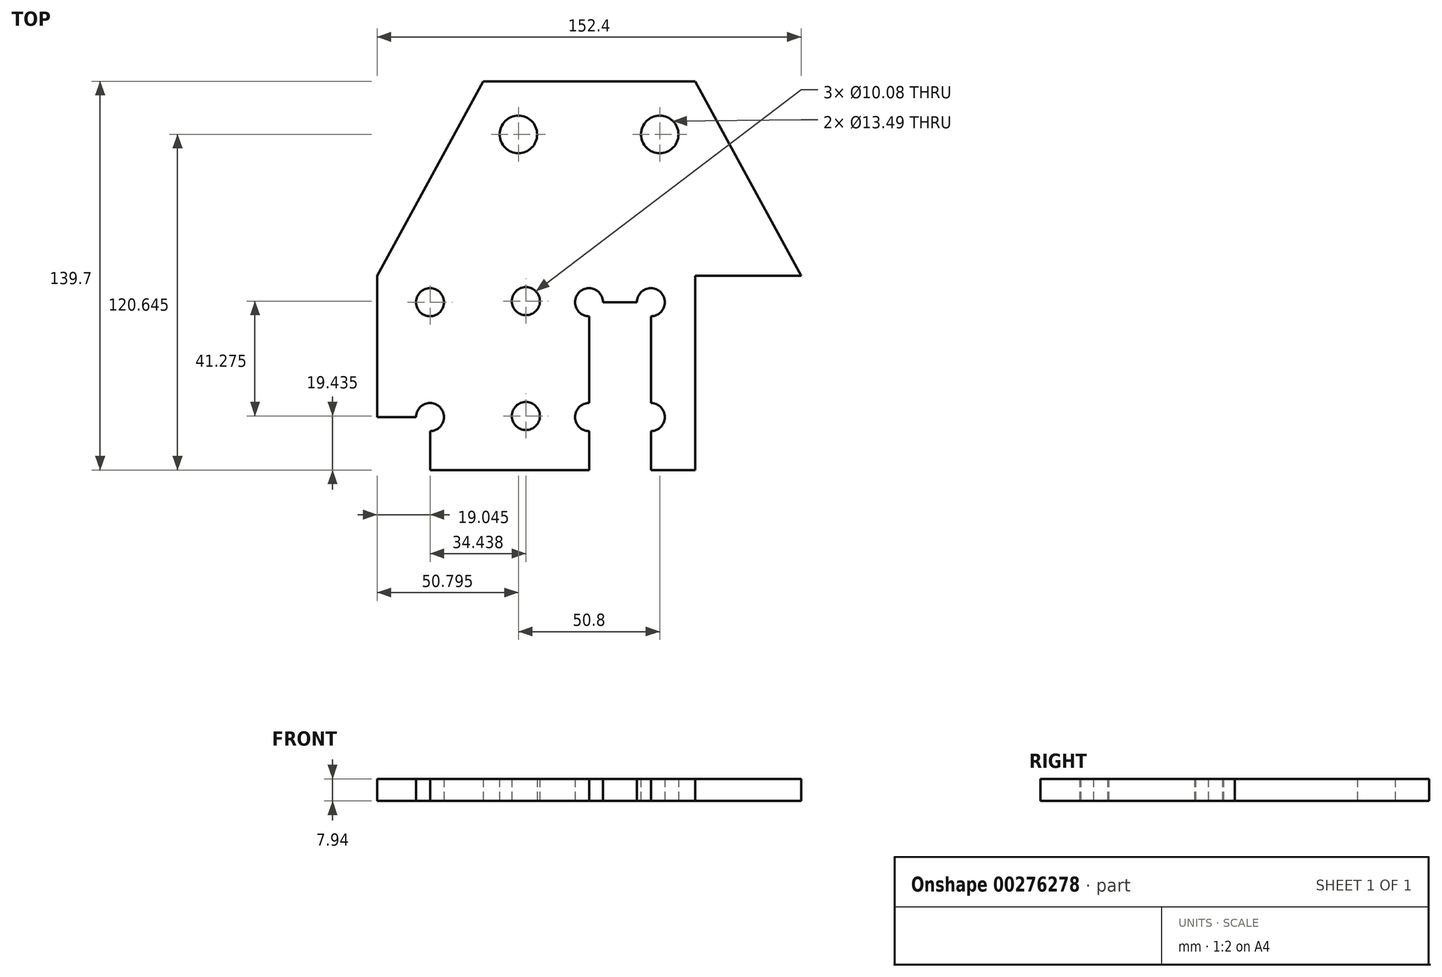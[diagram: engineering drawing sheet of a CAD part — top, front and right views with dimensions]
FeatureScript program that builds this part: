
annotation { "Feature Type Name" : "Feature", "Feature Type Description" : "" }
export const myFeature = defineFeature(function(context is Context, id is Id, definition is map)
    precondition{}
    {
        {
            var Q0;
            Q0=qCreatedBy(makeId("Top.planeOp"),FACE);
            var sketch = newSketch(context, id + "F0", { "sketchPlane" : qUnion([Q0])});
            skLineSegment(sketch, "E0.bottom", {"start": v(-76.05, -60.71) * mm, "end": v(76.35, -60.71) * mm});
            skLineSegment(sketch, "E0.top", {"start": v(-76.05, 78.99) * mm, "end": v(76.35, 78.99) * mm});
            skLineSegment(sketch, "E0.left", {"start": v(-76.05, -60.71) * mm, "end": v(-76.05, 78.99) * mm});
            skLineSegment(sketch, "E0.right", {"start": v(76.35, -60.71) * mm, "end": v(76.35, 78.99) * mm});
            skLineSegment(sketch, "E1", {"start": v(-76.05, -60.71) * mm, "end": v(-76.05, 9.14) * mm});
            skLineSegment(sketch, "E2", {"start": v(-76.05, 9.14) * mm, "end": v(76.35, 9.14) * mm});
            skLineSegment(sketch, "E3", {"start": v(76.35, 9.14) * mm, "end": v(76.35, -60.71) * mm});
            skLineSegment(sketch, "E4.bottom", {"start": v(-37.95, 78.99) * mm, "end": v(38.25, 78.99) * mm});
            skLineSegment(sketch, "E4.top", {"start": v(-37.95, -60.71) * mm, "end": v(38.25, -60.71) * mm});
            skLineSegment(sketch, "E4.left", {"start": v(-37.95, 78.99) * mm, "end": v(-37.95, -60.71) * mm});
            skLineSegment(sketch, "E4.right", {"start": v(38.25, 78.99) * mm, "end": v(38.25, -60.71) * mm});
            skLineSegment(sketch, "E5", {"start": v(-76.05, 78.99) * mm, "end": v(-37.95, 78.99) * mm});
            skLineSegment(sketch, "E6", {"start": v(-76.05, 9.14) * mm, "end": v(-37.95, 78.99) * mm});
            skLineSegment(sketch, "E7", {"start": v(38.25, 78.99) * mm, "end": v(76.35, 9.14) * mm});
            skPoint(sketch, "E8", {"position": v(38.25, 78.99) * mm});
            skLineSegment(sketch, "E9", {"start": v(-25.25, 59.94) * mm, "end": v(-25.25, 78.99) * mm});
            skLineSegment(sketch, "E10", {"start": v(25.55, 59.94) * mm, "end": v(25.55, 78.99) * mm});
            skLineSegment(sketch, "E11", {"start": v(-25.25, 59.94) * mm, "end": v(-37.95, 59.94) * mm});
            skLineSegment(sketch, "E12", {"start": v(25.55, 59.94) * mm, "end": v(38.25, 59.94) * mm});
            skLineSegment(sketch, "E13", {"start": v(-57, -0.39) * mm, "end": v(-57, -41.66) * mm});
            skLineSegment(sketch, "E14", {"start": v(-57, -41.66) * mm, "end": v(-76.05, -41.66) * mm});
            skLineSegment(sketch, "E15", {"start": v(-57, -41.66) * mm, "end": v(-57, -60.71) * mm});
            skLineSegment(sketch, "E16", {"start": v(57.3, -0.39) * mm, "end": v(57.3, -41.66) * mm});
            skLineSegment(sketch, "E17", {"start": v(57.3, -41.66) * mm, "end": v(57.3, -60.71) * mm});
            skLineSegment(sketch, "E18", {"start": v(57.3, -60.71) * mm, "end": v(76.35, -60.71) * mm});
            skLineSegment(sketch, "E19", {"start": v(-76.05, -60.71) * mm, "end": v(0.15, -60.71) * mm});
            skLineSegment(sketch, "E20", {"start": v(0.15, -0.39) * mm, "end": v(0.15, -41.66) * mm});
            skLineSegment(sketch, "E21", {"start": v(0.15, -41.66) * mm, "end": v(0.15, -60.71) * mm});
            skLineSegment(sketch, "E22", {"start": v(22.37, -0.39) * mm, "end": v(22.37, -41.66) * mm});
            skLineSegment(sketch, "E23", {"start": v(22.37, -41.66) * mm, "end": v(22.37, -60.71) * mm});
            skLineSegment(sketch, "E24", {"start": v(0.15, -0.39) * mm, "end": v(22.37, -0.39) * mm});
            skLineSegment(sketch, "E25", {"start": v(-22.57, 0) * mm, "end": v(-22.57, -41.28) * mm});
            skLineSegment(sketch, "E26", {"start": v(-22.57, -41.28) * mm, "end": v(-22.57, -60.33) * mm});
            skLineSegment(sketch, "E27", {"start": v(-22.57, 0) * mm, "end": v(-0.34, 0) * mm});
            skSolve(sketch);
        }
        {
            var Q0;
            {var subQ0=sQuery(id+"F0.wireOp",EDGE,"E6");Q0=makeQuery(id+"F0.imprint","IMPRINT",FACE,{"disambiguationData":[TD([[makeQuery(id+"F0.imprint","IMPRINT",EDGE,{"derivedFrom":subQ0}),-1.0]])]});}
            var Q1;
            {var subQ0=sQuery(id+"F0.wireOp",EDGE,"E1");Q1=makeQuery(id+"F0.imprint","IMPRINT",FACE,{"disambiguationData":[TD([[makeQuery(id+"F0.imprint","IMPRINT",EDGE,{"derivedFrom":subQ0}),-1.0]])]});}
            var Q2;
            {var subQ5=sQuery(id+"F0.wireOp",EDGE,"E4.top");Q2=makeQuery(id+"F0.imprint","IMPRINT",FACE,{"disambiguationData":[TD([[makeQuery(id+"F0.imprint","IMPRINT",EDGE,{"derivedFrom":subQ5}),1.0]])]});}
            var Q3;
            {var subQ3=sQuery(id+"F0.wireOp",EDGE,"E2");var subQ5=sQuery(id+"F0.wireOp",EDGE,"E4.left");var subQ6=makeQuery(id+"F0.imprint","INTERSECT",VERTEX,{"derivedFrom":[subQ3,subQ5]});Q3=makeQuery(id+"F0.imprint","IMPRINT",FACE,{"disambiguationData":[TD([[makeQuery(id+"F0.imprint","IMPRINT",EDGE,{"disambiguationData":[TD([[subQ6,-1.0]])],"derivedFrom":subQ3}),1.0]])]});}
            var Q4;
            {var subQ0=sQuery(id+"F0.wireOp",EDGE,"E9");var subQ1=sQuery(id+"F0.wireOp",EDGE,"LTa7V2wM-ZibM-cuZf-cZ65-yHtlyJLLMwwq");var subQ2=makeQuery(id+"F0.imprint","INTERSECT",VERTEX,{"derivedFrom":[subQ1,subQ0]});Q4=makeQuery(id+"F0.imprint","IMPRINT",FACE,{"disambiguationData":[TD([[makeQuery(id+"F0.imprint","IMPRINT",EDGE,{"disambiguationData":[TD([[subQ2,-1.0]])],"derivedFrom":subQ1}),-1.0]])]});}
            var Q5;
            {var subQ0=sQuery(id+"F0.wireOp",EDGE,"E10");var subQ1=sQuery(id+"F0.wireOp",EDGE,"ef0b0393-9919-4fb4-960b-99aeebce1d35");var subQ2=makeQuery(id+"F0.imprint","INTERSECT",VERTEX,{"derivedFrom":[subQ1,subQ0]});Q5=makeQuery(id+"F0.imprint","IMPRINT",FACE,{"disambiguationData":[TD([[makeQuery(id+"F0.imprint","IMPRINT",EDGE,{"disambiguationData":[TD([[subQ2,1.0]])],"derivedFrom":subQ1}),-1.0]])]});}
            var Q6;
            {var subQ0=sQuery(id+"F0.wireOp",EDGE,"E7");Q6=makeQuery(id+"F0.imprint","IMPRINT",FACE,{"disambiguationData":[TD([[makeQuery(id+"F0.imprint","IMPRINT",EDGE,{"derivedFrom":subQ0}),-1.0]])]});}
            var Q7;
            {var subQ0=sQuery(id+"F0.wireOp",EDGE,"E3");Q7=makeQuery(id+"F0.imprint","IMPRINT",FACE,{"disambiguationData":[TD([[makeQuery(id+"F0.imprint","IMPRINT",EDGE,{"derivedFrom":subQ0}),-1.0]])]});}
            var Q8;
            {var subQ7=sQuery(id+"F0.wireOp",EDGE,"E14");Q8=makeQuery(id+"F0.imprint","IMPRINT",FACE,{"disambiguationData":[TD([[makeQuery(id+"F0.imprint","IMPRINT",EDGE,{"derivedFrom":subQ7}),-1.0]])]});}
            var Q9;
            {var subQ3=sQuery(id+"F0.wireOp",EDGE,"E9");Q9=makeQuery(id+"F0.imprint","IMPRINT",FACE,{"disambiguationData":[TD([[makeQuery(id+"F0.imprint","IMPRINT",EDGE,{"derivedFrom":subQ3}),1.0]])]});}
            var Q10;
            {var subQ3=sQuery(id+"F0.wireOp",EDGE,"E10");Q10=makeQuery(id+"F0.imprint","IMPRINT",FACE,{"disambiguationData":[TD([[makeQuery(id+"F0.imprint","IMPRINT",EDGE,{"derivedFrom":subQ3}),-1.0]])]});}
            var Q11;
            Q11=makeQuery(id+"F0.imprint","IMPRINT",FACE,{"disambiguationData":[TD([[makeQuery(id+"F0.imprint","IMPRINT",EDGE,{"derivedFrom":sQuery(id+"F0.wireOp",EDGE,"E20")}),-1.0]])]});
            extrude(context, id + "F1", {"entities" : qUnion([Q0, Q1, Q2, Q3, Q4, Q5, Q6, Q7, Q8, Q9, Q10, Q11]), "depth" : 7.94 * mm});
        }
        {
            var Q0;
            Q0=sQuery(id+"F0.wireOp",VERTEX,"E13.start");
            var Q1;
            Q1=sQuery(id+"F0.wireOp",VERTEX,"E14.start");
            var Q2;
            Q2=sQuery(id+"F0.wireOp",VERTEX,"E20.start");
            var Q3;
            Q3=sQuery(id+"F0.wireOp",VERTEX,"E21.start");
            var Q4;
            Q4=sQuery(id+"F0.wireOp",VERTEX,"E16.start");
            var Q5;
            Q5=sQuery(id+"F0.wireOp",VERTEX,"E17.start");
            var Q6;
            Q6=sQuery(id+"F0.wireOp",VERTEX,"E25.start");
            var Q7;
            Q7=sQuery(id+"F0.wireOp",VERTEX,"E26.start");
            var Q8;
            Q8=sQuery(id+"F0.wireOp",VERTEX,"E23.start");
            var Q9;
            Q9=sQuery(id+"F0.wireOp",VERTEX,"E22.start");
            var Q10;
            Q10=makeQuery(id+"F1.opExtrude","SWEPT_BODY",BODY,{"disambiguationData":[OSD([sQuery(id+"F0.wireOp",EDGE,"E0.bottom"),sQuery(id+"F0.wireOp",EDGE,"E1"),sQuery(id+"F0.wireOp",EDGE,"E3"),sQuery(id+"F0.wireOp",EDGE,"E4.bottom"),sQuery(id+"F0.wireOp",EDGE,"E4.top"),sQuery(id+"F0.wireOp",EDGE,"E6"),sQuery(id+"F0.wireOp",EDGE,"E7"),sQuery(id+"F0.wireOp",EDGE,"LTa7V2wM-ZibM-cuZf-cZ65-yHtlyJLLMwwq"),sQuery(id+"F0.wireOp",EDGE,"ef0b0393-9919-4fb4-960b-99aeebce1d35"),sQuery(id+"F0.wireOp",EDGE,"E18"),sQuery(id+"F0.wireOp",EDGE,"E19")])]});
            hole(context, id + "F2", {"style" : HoleStyle.SIMPLE, "endStyle" : HoleEndStyle.THROUGH, "oppositeDirection" : true, "standardTappedOrClearance" : lookupTablePath({ "standard" : "ANSI", "fit" : "Normal (ASME)", "size" : "3/8", "type" : "Clearance" }), "standardBlindInLast" : lookupTablePath({ "fit" : "Free", "standard" : "ANSI", "size" : "3/8", "type" : "Clearance" }), "holeDiameter" : 10.08 * mm, "tappedDepth" : 12.7 * mm, "tapClearance" : 3, "locations" : qUnion([Q0, Q1, Q2, Q3, Q4, Q5, Q6, Q7, Q8, Q9]), "scope" : qUnion([Q10])});
        }
        {
            var Q0;
            Q0=sQuery(id+"F0.wireOp",VERTEX,"E9.start");
            var Q1;
            Q1=sQuery(id+"F0.wireOp",VERTEX,"E12.start");
            var Q2;
            Q2=makeQuery(id+"F1.opExtrude","SWEPT_BODY",BODY,{"disambiguationData":[OSD([sQuery(id+"F0.wireOp",EDGE,"E0.bottom"),sQuery(id+"F0.wireOp",EDGE,"E1"),sQuery(id+"F0.wireOp",EDGE,"E3"),sQuery(id+"F0.wireOp",EDGE,"E4.bottom"),sQuery(id+"F0.wireOp",EDGE,"E4.top"),sQuery(id+"F0.wireOp",EDGE,"E6"),sQuery(id+"F0.wireOp",EDGE,"E7"),sQuery(id+"F0.wireOp",EDGE,"E18"),sQuery(id+"F0.wireOp",EDGE,"E19")])]});
            hole(context, id + "F3", {"style" : HoleStyle.SIMPLE, "endStyle" : HoleEndStyle.THROUGH, "oppositeDirection" : true, "standardTappedOrClearance" : lookupTablePath({ "standard" : "ANSI", "fit" : "Normal (ASME)", "size" : "1/2", "type" : "Clearance" }), "standardBlindInLast" : lookupTablePath({ "fit" : "Free", "standard" : "ANSI", "size" : "1/2", "type" : "Clearance" }), "holeDiameter" : 13.5 * mm, "tappedDepth" : 12.7 * mm, "tapClearance" : 3, "locations" : qUnion([Q0, Q1]), "scope" : qUnion([Q2])});
        }
    });
